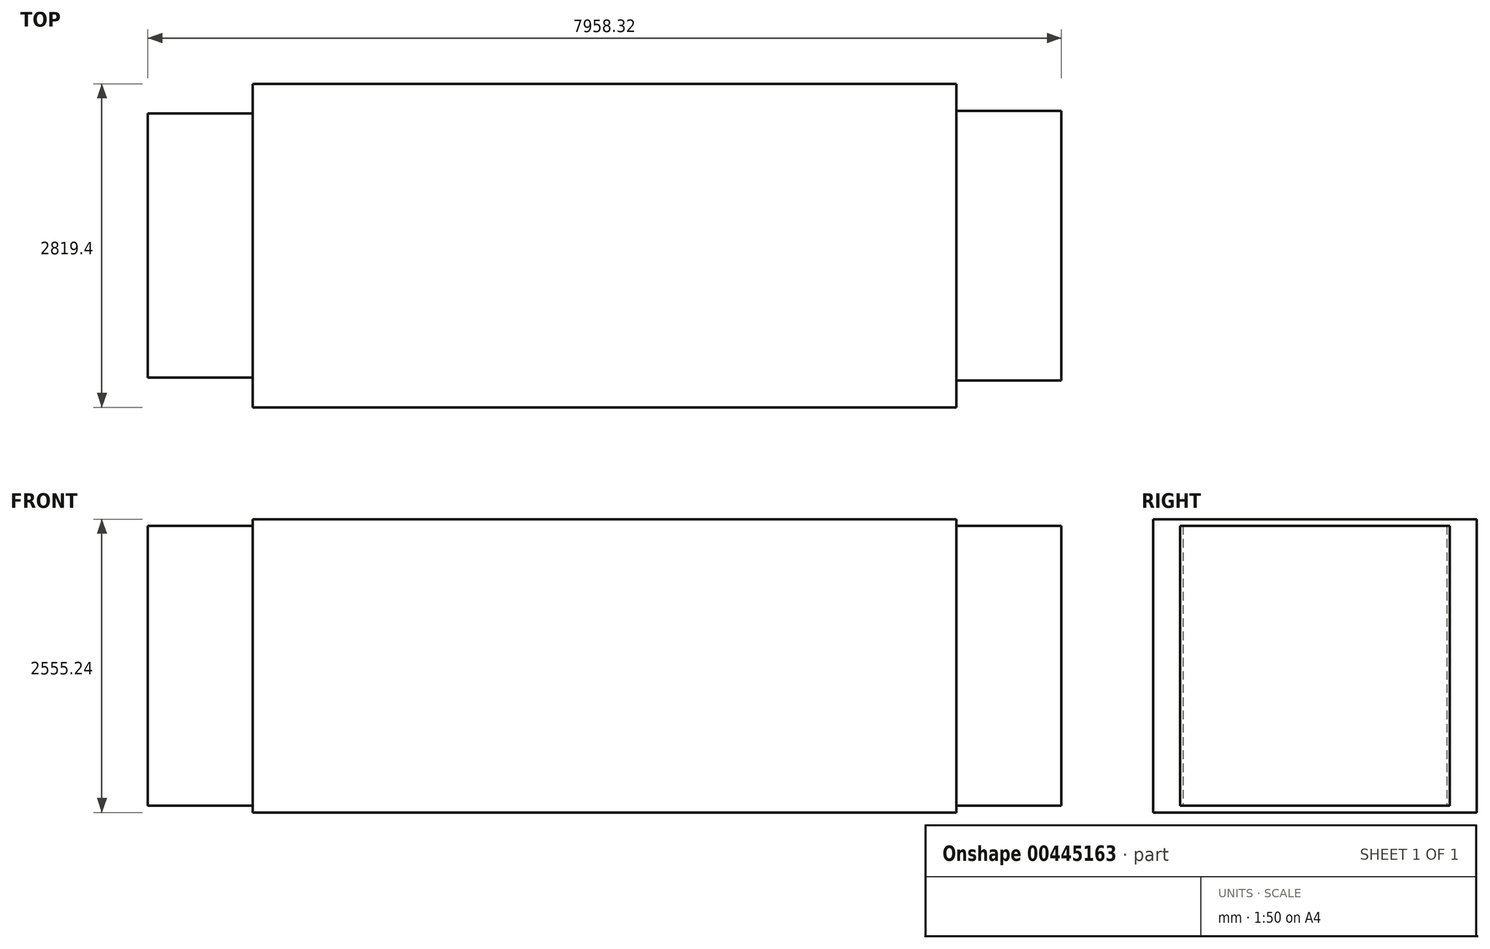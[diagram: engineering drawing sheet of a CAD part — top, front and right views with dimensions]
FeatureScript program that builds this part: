
annotation { "Feature Type Name" : "Feature", "Feature Type Description" : "" }
export const myFeature = defineFeature(function(context is Context, id is Id, definition is map)
    precondition{}
    {
        {
            var Q0;
            Q0=qCreatedBy(makeId("Top.planeOp"),FACE);
            var sketch = newSketch(context, id + "F0", { "sketchPlane" : qUnion([Q0])});
            skPoint(sketch, "E0.middle", {"position": v(0, 0) * mm});
            skLineSegment(sketch, "E1.bottom", {"start": v(3064.76, 1409.7) * mm, "end": v(-3064.76, 1409.7) * mm});
            skLineSegment(sketch, "E1.top", {"start": v(3064.76, -1409.7) * mm, "end": v(-3064.76, -1409.7) * mm});
            skLineSegment(sketch, "E1.left", {"start": v(3064.76, 1409.7) * mm, "end": v(3064.76, -1409.7) * mm});
            skLineSegment(sketch, "E1.right", {"start": v(-3064.76, 1409.7) * mm, "end": v(-3064.76, -1409.7) * mm});
            skSolve(sketch);
        }
        {
            var Q0;
            Q0 = qSketchRegion(id + "F0", true);
            extrude(context, id + "F1", {"entities" : qUnion([Q0]), "endBound" : BoundingType.SYMMETRIC, "depth" : 2555.24 * mm});
        }
        {
            var Q0;
            Q0=makeQuery(id+"F1.opExtrude","SWEPT_FACE",FACE,{"disambiguationData":[OSD([sQuery(id+"F0.wireOp",EDGE,"E1.left")])]});
            var sketch = newSketch(context, id + "F2", { "sketchPlane" : qUnion([Q0])});
            skPoint(sketch, "E2.middle", {"position": v(0, 0) * mm});
            skLineSegment(sketch, "E3.bottom", {"start": v(1174.81, 1219.2) * mm, "end": v(-1174.81, 1219.2) * mm});
            skLineSegment(sketch, "E3.top", {"start": v(1174.81, -1219.2) * mm, "end": v(-1174.81, -1219.2) * mm});
            skLineSegment(sketch, "E3.left", {"start": v(1174.81, 1219.2) * mm, "end": v(1174.81, -1219.2) * mm});
            skLineSegment(sketch, "E3.right", {"start": v(-1174.81, 1219.2) * mm, "end": v(-1174.81, -1219.2) * mm});
            skSolve(sketch);
        }
        {
            var Q0;
            Q0=makeQuery(id+"F2.imprint","IMPRINT",FACE,{"disambiguationData":[TD([[makeQuery(id+"F2.imprint","IMPRINT",EDGE,{"derivedFrom":sQuery(id+"F2.wireOp",EDGE,"E3.bottom")}),1.0]])]});
            extrude(context, id + "F3", {"entities" : qUnion([Q0]), "operationType" : NewBodyOperationType.ADD, "depth" : 914.4 * mm});
        }
        {
            var Q0;
            Q0=makeQuery(id+"F1.opExtrude","SWEPT_FACE",FACE,{"disambiguationData":[OSD([sQuery(id+"F0.wireOp",EDGE,"E1.right")])]});
            var sketch = newSketch(context, id + "F4", { "sketchPlane" : qUnion([Q0])});
            skLineSegment(sketch, "E4.bottom", {"start": v(1150.62, 1219.2) * mm, "end": v(-1150.62, 1219.2) * mm});
            skLineSegment(sketch, "E4.top", {"start": v(1150.62, -1219.2) * mm, "end": v(-1150.62, -1219.2) * mm});
            skLineSegment(sketch, "E4.left", {"start": v(1150.62, 1219.2) * mm, "end": v(1150.62, -1219.2) * mm});
            skLineSegment(sketch, "E4.right", {"start": v(-1150.62, 1219.2) * mm, "end": v(-1150.62, -1219.2) * mm});
            skPoint(sketch, "E4.middle", {"position": v(0, 0) * mm});
            skSolve(sketch);
        }
        {
            var Q0;
            Q0 = qSketchRegion(id + "F4", true);
            extrude(context, id + "F5", {"entities" : qUnion([Q0]), "operationType" : NewBodyOperationType.ADD, "depth" : 914.4 * mm});
        }
    });
